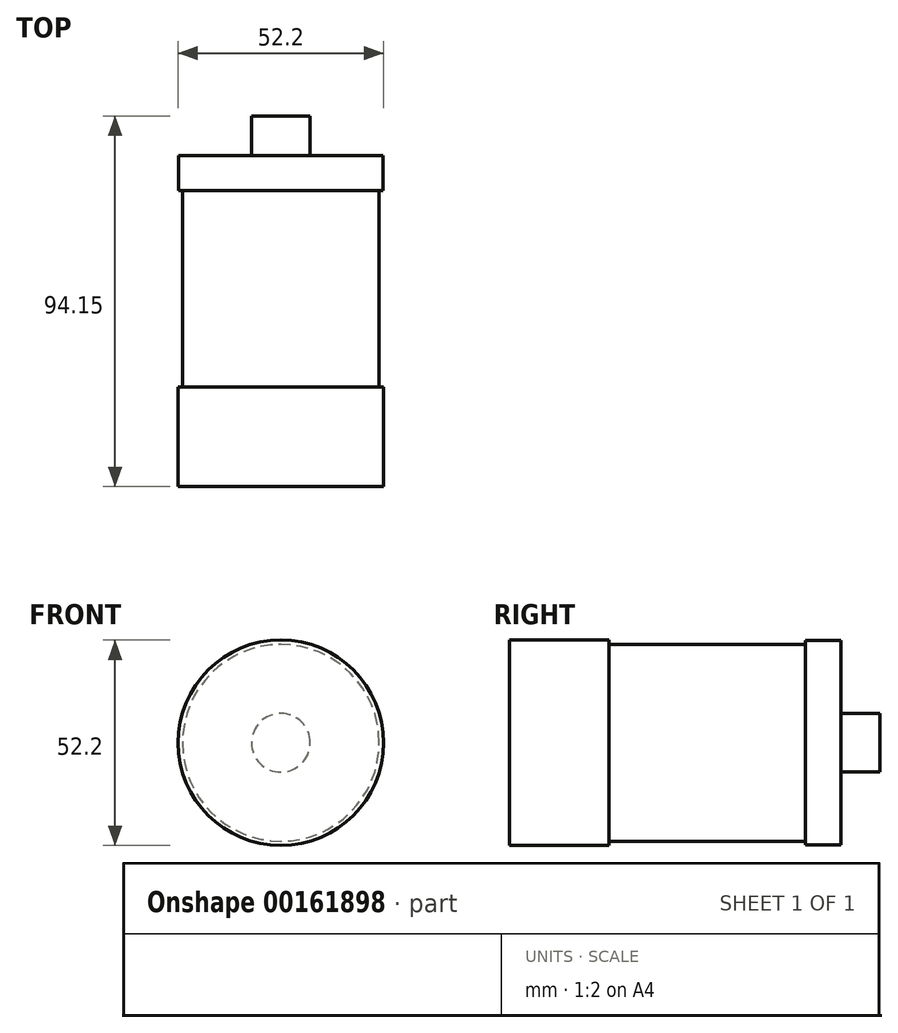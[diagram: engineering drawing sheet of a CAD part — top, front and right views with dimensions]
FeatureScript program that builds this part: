
annotation { "Feature Type Name" : "Feature", "Feature Type Description" : "" }
export const myFeature = defineFeature(function(context is Context, id is Id, definition is map)
    precondition{}
    {
        {
            var Q0;
            Q0=qCreatedBy(makeId("Front.planeOp"),FACE);
            var sketch = newSketch(context, id + "F0", { "sketchPlane" : qUnion([Q0])});
            skCircle(sketch, "E0", {"center": v(0, 0) * mm, "radius": 26.1 * mm});
            skLineSegment(sketch, "E1", {"start": v(0, 0) * mm, "end": v(26.1, 0) * mm});
            skLineSegment(sketch, "E2", {"start": v(26.1, 0) * mm, "end": v(-26.1, 0) * mm});
            skSolve(sketch);
        }
        {
            var Q0;
            Q0=makeQuery(id+"F0.imprint","IMPRINT",FACE,{"disambiguationData":[TD([[makeQuery(id+"F0.imprint","IMPRINT",EDGE,{"derivedFrom":sQuery(id+"F0.wireOp",EDGE,"E0")}),1.0]])]});
            extrude(context, id + "F1", {"entities" : qUnion([Q0]), "oppositeDirection" : true, "depth" : 25.25 * mm});
        }
        {
            var Q0;
            Q0=makeQuery(id+"F1.opExtrude","CAP_FACE",FACE,{"disambiguationData":[OSD([sQuery(id+"F0.wireOp",EDGE,"E0")])],"isStart":false});
            var sketch = newSketch(context, id + "F2", { "sketchPlane" : qUnion([Q0])});
            skCircle(sketch, "E3", {"center": v(0, 0) * mm, "radius": 25 * mm});
            skSolve(sketch);
        }
        {
            var Q0;
            Q0 = qSketchRegion(id + "F2", true);
            extrude(context, id + "F3", {"entities" : qUnion([Q0]), "operationType" : NewBodyOperationType.ADD, "depth" : 49.9 * mm});
        }
        {
            var Q0;
            Q0=makeQuery(id+"F3.opExtrude","CAP_FACE",FACE,{"disambiguationData":[OSD([sQuery(id+"F2.wireOp",EDGE,"E3")])],"isStart":false});
            var sketch = newSketch(context, id + "F4", { "sketchPlane" : qUnion([Q0])});
            skCircle(sketch, "E4", {"center": v(0, 0) * mm, "radius": 26 * mm});
            skSolve(sketch);
        }
        {
            var Q0;
            Q0 = qSketchRegion(id + "F4", true);
            extrude(context, id + "F5", {"entities" : qUnion([Q0]), "operationType" : NewBodyOperationType.ADD, "depth" : 9 * mm});
        }
        {
            var Q0;
            Q0=makeQuery(id+"F5.opExtrude","CAP_FACE",FACE,{"disambiguationData":[OSD([sQuery(id+"F4.wireOp",EDGE,"E4")])],"isStart":false});
            var sketch = newSketch(context, id + "F6", { "sketchPlane" : qUnion([Q0])});
            skCircle(sketch, "E5", {"center": v(0, 0) * mm, "radius": 7.45 * mm});
            skSolve(sketch);
        }
        {
            var Q0;
            Q0 = qSketchRegion(id + "F6", true);
            extrude(context, id + "F7", {"entities" : qUnion([Q0]), "operationType" : NewBodyOperationType.ADD, "depth" : 10 * mm});
        }
    });
